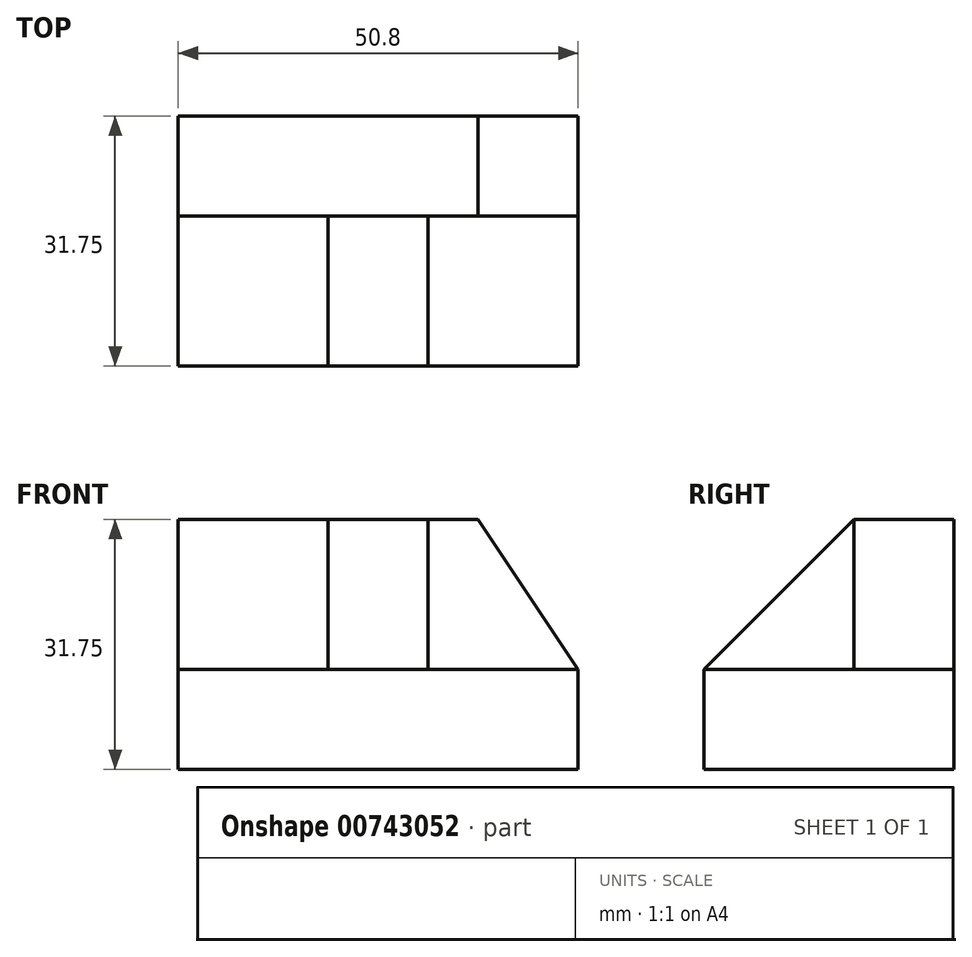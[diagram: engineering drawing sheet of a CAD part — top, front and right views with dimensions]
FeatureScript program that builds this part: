
annotation { "Feature Type Name" : "Feature", "Feature Type Description" : "" }
export const myFeature = defineFeature(function(context is Context, id is Id, definition is map)
    precondition{}
    {
        {
            var Q0;
            Q0=qCreatedBy(makeId("Front.planeOp"),FACE);
            var sketch = newSketch(context, id + "F0", { "sketchPlane" : qUnion([Q0])});
            skLineSegment(sketch, "E0", {"start": v(0, 0) * mm, "end": v(0, 31.75) * mm});
            skLineSegment(sketch, "E1", {"start": v(0, 31.75) * mm, "end": v(50.8, 31.75) * mm});
            skLineSegment(sketch, "E2", {"start": v(50.8, 31.75) * mm, "end": v(50.8, 0) * mm});
            skLineSegment(sketch, "E3", {"start": v(50.8, 0) * mm, "end": v(0, 0) * mm});
            skSolve(sketch);
        }
        {
            var Q0;
            Q0 = qSketchRegion(id + "F0", true);
            extrude(context, id + "F1", {"entities" : qUnion([Q0]), "oppositeDirection" : true, "depth" : 31.75 * mm, "offsetDistance" : 25.4 * mm});
        }
        {
            var Q0;
            Q0=makeQuery(id+"F1.opExtrude","SWEPT_FACE",FACE,{"disambiguationData":[OSD([sQuery(id+"F0.wireOp",EDGE,"E0")])]});
            var sketch = newSketch(context, id + "F2", { "sketchPlane" : qUnion([Q0])});
            skLineSegment(sketch, "E4", {"start": v(-19.05, 31.75) * mm, "end": v(-19.05, 12.7) * mm});
            skLineSegment(sketch, "E5", {"start": v(-19.05, 12.7) * mm, "end": v(0, 12.7) * mm});
            skSolve(sketch);
        }
        {
            var Q0;
            {var subQ0=sQuery(id+"F2.wireOp",EDGE,"E4");Q0=makeQuery(id+"F2.imprint","IMPRINT",FACE,{"disambiguationData":[TD([[makeQuery(id+"F2.imprint","IMPRINT",EDGE,{"derivedFrom":subQ0}),1.0]])]});}
            extrude(context, id + "F3", {"entities" : qUnion([Q0]), "operationType" : NewBodyOperationType.REMOVE, "oppositeDirection" : true, "depth" : 19.05 * mm, "offsetDistance" : 25.4 * mm});
        }
        {
            var Q0;
            Q0=makeQuery(id+"F1.opExtrude","SWEPT_FACE",FACE,{"disambiguationData":[OSD([sQuery(id+"F0.wireOp",EDGE,"E2")])]});
            var sketch = newSketch(context, id + "F4", { "sketchPlane" : qUnion([Q0])});
            skLineSegment(sketch, "E6", {"start": v(19.05, 31.75) * mm, "end": v(19.05, 12.7) * mm});
            skLineSegment(sketch, "E7", {"start": v(19.05, 12.7) * mm, "end": v(0, 12.7) * mm});
            skSolve(sketch);
        }
        {
            var Q0;
            {var subQ0=sQuery(id+"F4.wireOp",EDGE,"E6");Q0=makeQuery(id+"F4.imprint","IMPRINT",FACE,{"disambiguationData":[TD([[makeQuery(id+"F4.imprint","IMPRINT",EDGE,{"derivedFrom":subQ0}),-1.0]])]});}
            extrude(context, id + "F5", {"entities" : qUnion([Q0]), "operationType" : NewBodyOperationType.REMOVE, "oppositeDirection" : true, "depth" : 19.05 * mm, "offsetDistance" : 25.4 * mm});
        }
        {
            var Q0;
            Q0=makeQuery(id+"F5.boolean.opBoolean","COPY",FACE,{"derivedFrom":makeQuery(id+"F5.opExtrude","CAP_FACE",FACE,{"disambiguationData":[OSD([sQuery(id+"F0.wireOp",EDGE,"E1"),sQuery(id+"F0.wireOp",EDGE,"E2"),sQuery(id+"F4.wireOp",EDGE,"E6"),sQuery(id+"F4.wireOp",EDGE,"E7")])],"isStart":false})});
            var sketch = newSketch(context, id + "F6", { "sketchPlane" : qUnion([Q0])});
            skLineSegment(sketch, "E8", {"start": v(19.05, 31.75) * mm, "end": v(0, 12.7) * mm});
            skSolve(sketch);
        }
        {
            var Q0;
            Q0=makeQuery(id+"F6.imprint","IMPRINT",FACE,{"disambiguationData":[TD([[makeQuery(id+"F6.imprint","IMPRINT",EDGE,{"derivedFrom":sQuery(id+"F6.wireOp",EDGE,"E8")}),-1.0]])]});
            extrude(context, id + "F7", {"entities" : qUnion([Q0]), "operationType" : NewBodyOperationType.REMOVE, "oppositeDirection" : true, "depth" : 25.4 * mm, "offsetDistance" : 25.4 * mm});
        }
        {
            var Q0;
            Q0=makeQuery(id+"F5.boolean.opBoolean","COPY",FACE,{"derivedFrom":makeQuery(id+"F5.opExtrude","SWEPT_FACE",FACE,{"disambiguationData":[OSD([sQuery(id+"F4.wireOp",EDGE,"E6")])]})});
            var sketch = newSketch(context, id + "F8", { "sketchPlane" : qUnion([Q0])});
            skLineSegment(sketch, "E9", {"start": v(38.1, 31.75) * mm, "end": v(50.8, 12.7) * mm});
            skSolve(sketch);
        }
        {
            var Q0;
            {var subQ0=sQuery(id+"F8.wireOp",EDGE,"E9");Q0=makeQuery(id+"F8.imprint","IMPRINT",FACE,{"disambiguationData":[TD([[makeQuery(id+"F8.imprint","IMPRINT",EDGE,{"derivedFrom":subQ0}),1.0]])]});}
            extrude(context, id + "F9", {"entities" : qUnion([Q0]), "operationType" : NewBodyOperationType.REMOVE, "oppositeDirection" : true, "depth" : 25.4 * mm, "offsetDistance" : 25.4 * mm});
        }
    });
